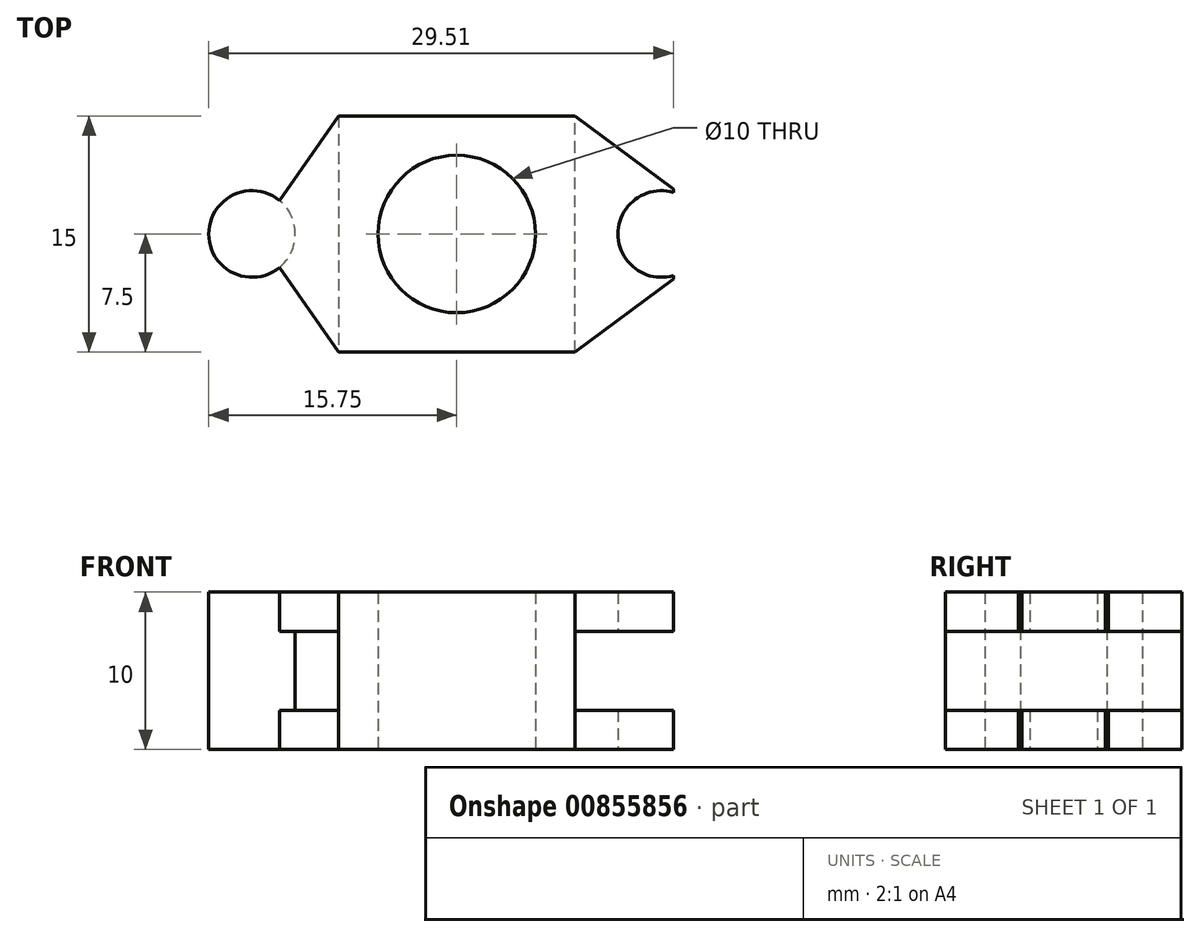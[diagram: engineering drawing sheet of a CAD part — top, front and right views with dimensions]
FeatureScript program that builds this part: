
annotation { "Feature Type Name" : "Feature", "Feature Type Description" : "" }
export const myFeature = defineFeature(function(context is Context, id is Id, definition is map)
    precondition{}
    {
        {
            var Q0;
            Q0=qCreatedBy(makeId("Top.planeOp"),FACE);
            var sketch = newSketch(context, id + "F0", { "sketchPlane" : qUnion([Q0])});
            skLineSegment(sketch, "E0.bottom", {"start": v(7.5, 7.5) * mm, "end": v(-7.5, 7.5) * mm});
            skLineSegment(sketch, "E0.top", {"start": v(7.5, -7.5) * mm, "end": v(-7.5, -7.5) * mm});
            skLineSegment(sketch, "E0.left", {"start": v(7.5, 7.5) * mm, "end": v(7.5, -7.5) * mm});
            skLineSegment(sketch, "E0.right", {"start": v(-7.5, 7.5) * mm, "end": v(-7.5, -7.5) * mm});
            skPoint(sketch, "E0.middle", {"position": v(0, 0) * mm});
            skCircle(sketch, "E1", {"center": v(0, 0) * mm, "radius": 5 * mm});
            skSolve(sketch);
        }
        {
            var Q0;
            Q0 = qSketchRegion(id + "F0", true);
            extrude(context, id + "F1", {"entities" : qUnion([Q0]), "endBound" : BoundingType.SYMMETRIC, "depth" : 10 * mm, "offsetDistance" : 25 * mm});
        }
        {
            var Q0;
            Q0=qCreatedBy(makeId("Top.planeOp"),FACE);
            var sketch = newSketch(context, id + "F2", { "sketchPlane" : qUnion([Q0])});
            skLineSegment(sketch, "E2.0", {"start": v(7.5, 7.5) * mm, "end": v(7.5, -7.5) * mm});
            skLineSegment(sketch, "E3", {"start": v(7.5, 7.5) * mm, "end": v(13.76, 2.86) * mm});
            skLineSegment(sketch, "E4", {"start": v(13.76, -2.86) * mm, "end": v(7.5, -7.5) * mm});
            skArc(sketch, "E5", {"start": v(13.76, 2.64) * mm, "mid": v(10.25, 0) * mm, "end": v(13.76, -2.64) * mm});
            skPoint(sketch, "E6.orphan", {"position": v(17.62, 0) * mm});
            skLineSegment(sketch, "E7", {"start": v(13.76, 4.26) * mm, "end": v(13.76, -5.13) * mm, "construction": true});
            skLineSegment(sketch, "E8", {"start": v(13.76, 2.86) * mm, "end": v(13.76, 2.64) * mm});
            skLineSegment(sketch, "E9", {"start": v(13.76, -2.64) * mm, "end": v(13.76, -2.86) * mm});
            skSolve(sketch);
        }
        {
            var Q0;
            Q0 = qSketchRegion(id + "F2", true);
            extrude(context, id + "F3", {"entities" : qUnion([Q0]), "operationType" : NewBodyOperationType.ADD, "endBound" : BoundingType.SYMMETRIC, "depth" : 10 * mm, "offsetDistance" : 25 * mm});
        }
        {
            var Q0;
            Q0=qCreatedBy(makeId("Top.planeOp"),FACE);
            var sketch = newSketch(context, id + "F4", { "sketchPlane" : qUnion([Q0])});
            skArc(sketch, "E10", {"start": v(-11.26, 2.13) * mm, "mid": v(-15.75, 0) * mm, "end": v(-11.26, -2.13) * mm});
            skLineSegment(sketch, "E11.0", {"start": v(-7.5, 7.5) * mm, "end": v(-7.5, -7.5) * mm});
            skLineSegment(sketch, "E12", {"start": v(-11.26, 2.13) * mm, "end": v(-7.5, 7.5) * mm});
            skLineSegment(sketch, "E13", {"start": v(-11.26, -2.13) * mm, "end": v(-7.5, -7.5) * mm});
            skSolve(sketch);
        }
        {
            var Q0;
            Q0 = qSketchRegion(id + "F4", true);
            extrude(context, id + "F5", {"entities" : qUnion([Q0]), "operationType" : NewBodyOperationType.ADD, "endBound" : BoundingType.SYMMETRIC, "depth" : 10 * mm, "offsetDistance" : 25 * mm});
        }
        {
            var Q0;
            Q0=qCreatedBy(makeId("Top.planeOp"),FACE);
            var sketch = newSketch(context, id + "F6", { "sketchPlane" : qUnion([Q0])});
            skPoint(sketch, "E14.0", {"position": v(13.76, 2.86) * mm});
            skPoint(sketch, "E15.0", {"position": v(13.76, -2.86) * mm});
            skPoint(sketch, "E16.0", {"position": v(-7.5, 7.5) * mm});
            skPoint(sketch, "E17.0", {"position": v(-7.5, -7.5) * mm});
            skLineSegment(sketch, "E18", {"start": v(-7.5, 2.13) * mm, "end": v(-7.5, 7.5) * mm});
            skLineSegment(sketch, "E19.MirrorCS", {"start": v(-7.5, -2.13) * mm, "end": v(-7.5, -7.5) * mm});
            skPoint(sketch, "E20.0", {"position": v(7.5, 7.5) * mm});
            skLineSegment(sketch, "E21", {"start": v(7.5, 2.86) * mm, "end": v(7.5, 7.5) * mm});
            skLineSegment(sketch, "E22.MirrorCS", {"start": v(7.5, -2.86) * mm, "end": v(7.5, -7.5) * mm});
            skPoint(sketch, "E23.MirrorP", {"position": v(7.5, -7.5) * mm});
            skLineSegment(sketch, "E24", {"start": v(-11.26, 2.13) * mm, "end": v(-11.26, 7.5) * mm});
            skLineSegment(sketch, "E25", {"start": v(-11.26, 7.5) * mm, "end": v(-7.5, 7.5) * mm});
            skLineSegment(sketch, "E26", {"start": v(-11.26, -2.13) * mm, "end": v(-11.26, -7.5) * mm});
            skLineSegment(sketch, "E27", {"start": v(-11.26, -7.5) * mm, "end": v(-7.5, -7.5) * mm});
            skLineSegment(sketch, "E28", {"start": v(7.5, -7.5) * mm, "end": v(13.76, -7.5) * mm});
            skLineSegment(sketch, "E29", {"start": v(13.76, -7.5) * mm, "end": v(13.76, -2.86) * mm});
            skLineSegment(sketch, "E30", {"start": v(13.76, 2.86) * mm, "end": v(13.76, 7.5) * mm});
            skLineSegment(sketch, "E31", {"start": v(13.76, 7.5) * mm, "end": v(7.5, 7.5) * mm});
            skLineSegment(sketch, "E32", {"start": v(7.5, 2.86) * mm, "end": v(7.5, -2.86) * mm});
            skLineSegment(sketch, "E33", {"start": v(13.76, 2.86) * mm, "end": v(13.76, -2.86) * mm});
            skLineSegment(sketch, "E34", {"start": v(-7.5, 2.13) * mm, "end": v(-7.5, -2.13) * mm});
            skPoint(sketch, "E35.MirrorCS.start.orphan", {"position": v(-11.26, -2.13) * mm});
            skArc(sketch, "E36", {"start": v(-11.26, -2.13) * mm, "mid": v(-10.25, 0) * mm, "end": v(-11.26, 2.13) * mm});
            skSolve(sketch);
        }
        {
            var Q0;
            Q0 = qSketchRegion(id + "F6", true);
            extrude(context, id + "F7", {"entities" : qUnion([Q0]), "operationType" : NewBodyOperationType.REMOVE, "endBound" : BoundingType.SYMMETRIC, "oppositeDirection" : true, "depth" : 5 * mm, "offsetDistance" : 25 * mm});
        }
    });
